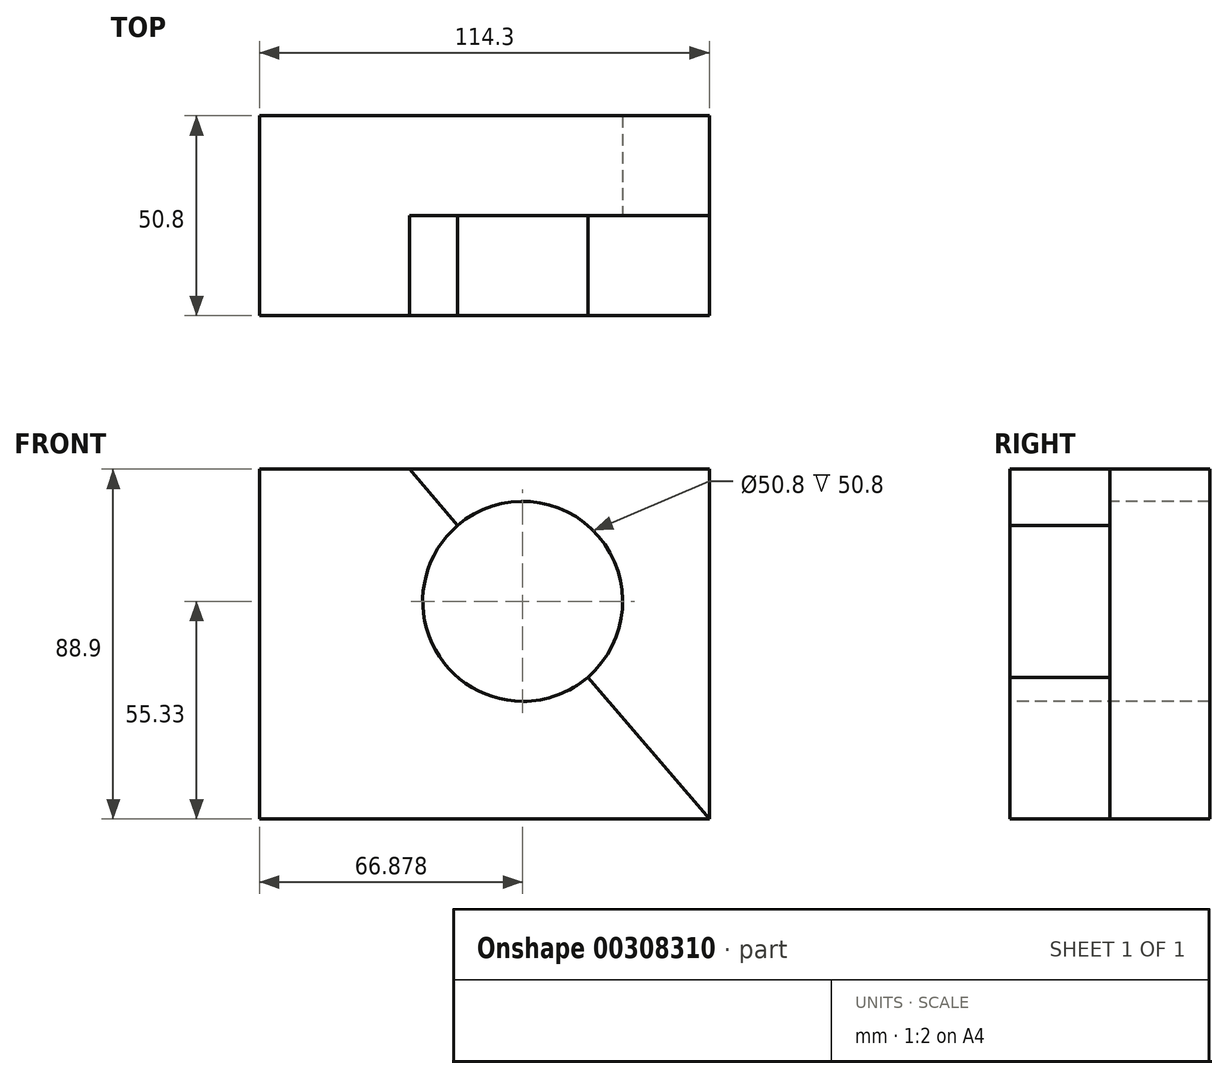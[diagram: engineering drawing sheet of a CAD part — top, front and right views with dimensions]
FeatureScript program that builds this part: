
annotation { "Feature Type Name" : "Feature", "Feature Type Description" : "" }
export const myFeature = defineFeature(function(context is Context, id is Id, definition is map)
    precondition{}
    {
        {
            var Q0;
            Q0=qCreatedBy(makeId("Right.planeOp"),FACE);
            var sketch = newSketch(context, id + "F0", { "sketchPlane" : qUnion([Q0])});
            skLineSegment(sketch, "E0", {"start": v(-15.68, -26.39) * mm, "end": v(9.72, -26.39) * mm});
            skLineSegment(sketch, "E1", {"start": v(-15.68, -26.39) * mm, "end": v(-15.68, 62.51) * mm});
            skLineSegment(sketch, "E2", {"start": v(-15.68, 62.51) * mm, "end": v(9.72, 62.51) * mm});
            skLineSegment(sketch, "E3", {"start": v(9.72, 62.51) * mm, "end": v(9.72, -26.39) * mm});
            skSolve(sketch);
        }
        {
            var Q0;
            Q0=makeQuery(id+"F0.imprint","IMPRINT",FACE,{"disambiguationData":[TD([[makeQuery(id+"F0.imprint","IMPRINT",EDGE,{"derivedFrom":sQuery(id+"F0.wireOp",EDGE,"E0")}),1.0]])]});
            extrude(context, id + "F1", {"entities" : qUnion([Q0]), "oppositeDirection" : true, "depth" : 114.3 * mm});
        }
        {
            var Q0;
            Q0=makeQuery(id+"F1.opExtrude","SWEPT_FACE",FACE,{"disambiguationData":[OSD([sQuery(id+"F0.wireOp",EDGE,"E1")])]});
            var sketch = newSketch(context, id + "F2", { "sketchPlane" : qUnion([Q0])});
            skLineSegment(sketch, "E4", {"start": v(-114.3, 62.51) * mm, "end": v(-76.2, 62.51) * mm});
            skLineSegment(sketch, "E5", {"start": v(-76.2, 62.51) * mm, "end": v(0, -26.39) * mm});
            skSolve(sketch);
        }
        {
            var Q0;
            Q0=makeQuery(id+"F2.imprint","IMPRINT",FACE,{"disambiguationData":[TD([[makeQuery(id+"F2.imprint","IMPRINT",EDGE,{"derivedFrom":sQuery(id+"F2.wireOp",EDGE,"E4")}),-1.0]])]});
            extrude(context, id + "F3", {"entities" : qUnion([Q0]), "operationType" : NewBodyOperationType.ADD, "depth" : 25.4 * mm});
        }
        {
            var Q0;
            Q0=makeQuery(id+"F3.opExtrude","CAP_FACE",FACE,{"disambiguationData":[OSD([sQuery(id+"F0.wireOp",EDGE,"E0"),sQuery(id+"F0.wireOp",EDGE,"E1"),sQuery(id+"F2.wireOp",EDGE,"E4"),sQuery(id+"F2.wireOp",EDGE,"E5")])],"isStart":false});
            var sketch = newSketch(context, id + "F4", { "sketchPlane" : qUnion([Q0])});
            skCircle(sketch, "E6", {"center": v(-47.42, 28.94) * mm, "radius": 25.4 * mm});
            skSolve(sketch);
        }
        {
            var Q0;
            {var subQ0=sQuery(id+"F4.wireOp",EDGE,"E6");var subQ1=makeQuery(id+"F3.opExtrude","CAP_EDGE",EDGE,{"disambiguationData":[OSD([sQuery(id+"F2.wireOp",EDGE,"E5")])],"isStart":false});var subQ2=makeQuery(id+"F4.imprint","INTERSECT",VERTEX,{"disambiguationData":[OD(0.0)],"derivedFrom":[subQ1,subQ0]});Q0=makeQuery(id+"F4.imprint","IMPRINT",FACE,{"disambiguationData":[TD([[makeQuery(id+"F4.imprint","IMPRINT",EDGE,{"disambiguationData":[TD([[subQ2,-1.0]])],"derivedFrom":subQ0}),1.0]])]});}
            var Q1;
            {var subQ0=sQuery(id+"F4.wireOp",EDGE,"E6");var subQ1=makeQuery(id+"F3.opExtrude","CAP_EDGE",EDGE,{"disambiguationData":[OSD([sQuery(id+"F2.wireOp",EDGE,"E5")])],"isStart":false});var subQ2=makeQuery(id+"F4.imprint","INTERSECT",VERTEX,{"disambiguationData":[OD(0.0)],"derivedFrom":[subQ1,subQ0]});Q1=makeQuery(id+"F4.imprint","IMPRINT",FACE,{"disambiguationData":[TD([[makeQuery(id+"F4.imprint","IMPRINT",EDGE,{"disambiguationData":[TD([[subQ2,1.0]])],"derivedFrom":subQ0}),1.0]])]});}
            extrude(context, id + "F5", {"entities" : qUnion([Q0, Q1]), "operationType" : NewBodyOperationType.REMOVE, "endBound" : BoundingType.THROUGH_ALL, "oppositeDirection" : true, "depth" : 25.4 * mm});
        }
    });
